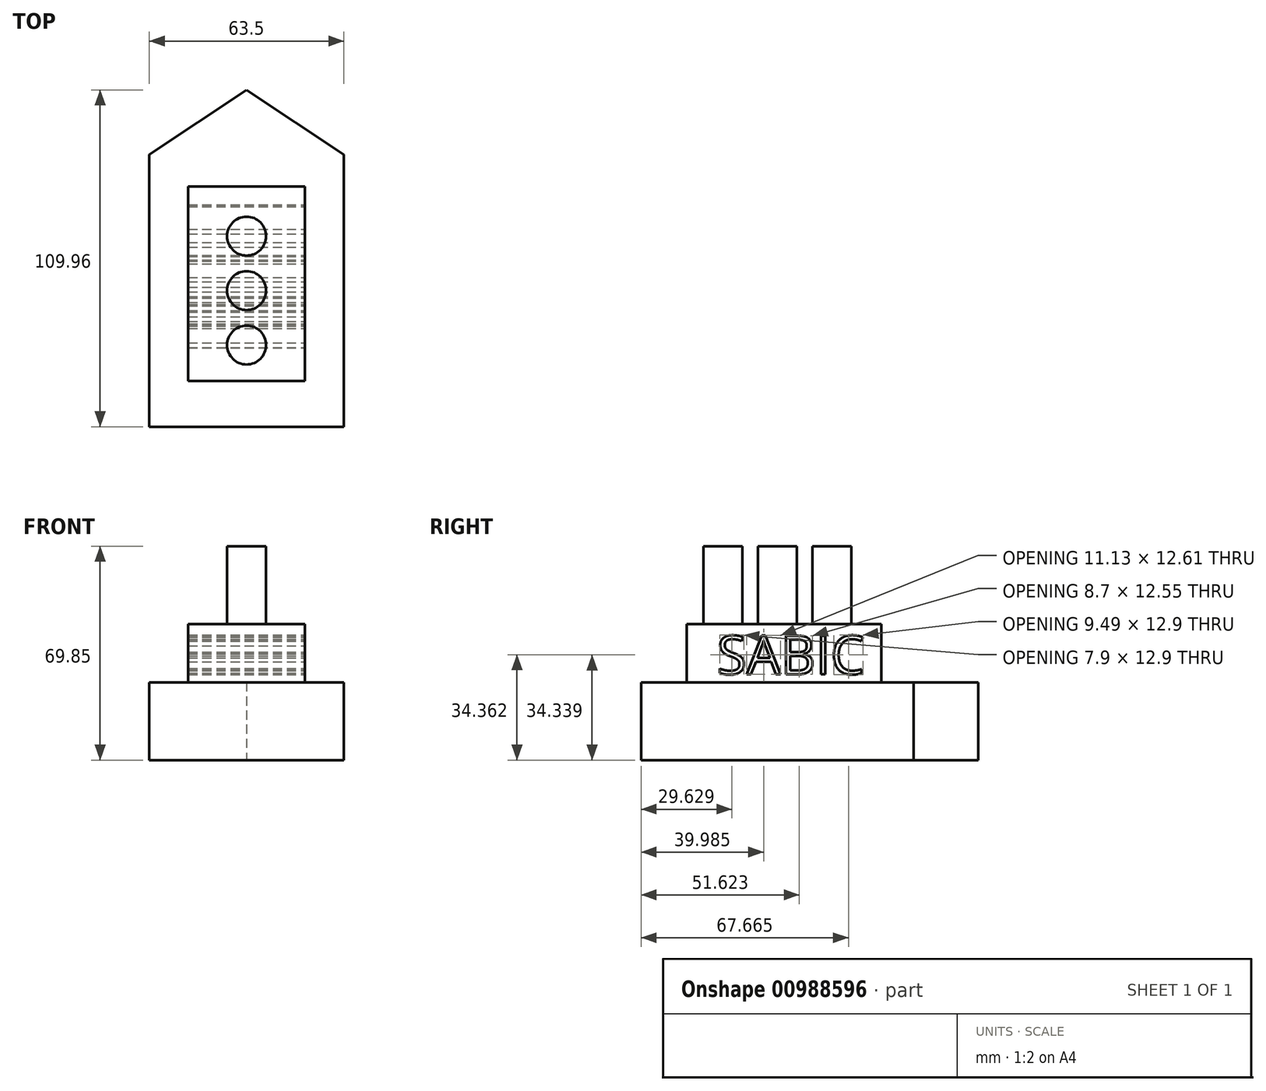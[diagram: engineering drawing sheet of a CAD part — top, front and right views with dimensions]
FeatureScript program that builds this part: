
annotation { "Feature Type Name" : "Feature", "Feature Type Description" : "" }
export const myFeature = defineFeature(function(context is Context, id is Id, definition is map)
    precondition{}
    {
        {
            var Q0;
            Q0=qCreatedBy(makeId("Top.planeOp"),FACE);
            var sketch = newSketch(context, id + "F0", { "sketchPlane" : qUnion([Q0])});
            skLineSegment(sketch, "E0", {"start": v(-31.75, 38.66) * mm, "end": v(-31.75, -50.24) * mm});
            skLineSegment(sketch, "E1", {"start": v(-31.75, -50.24) * mm, "end": v(31.75, -50.24) * mm});
            skLineSegment(sketch, "E2", {"start": v(31.75, -50.24) * mm, "end": v(31.75, 38.66) * mm});
            skLineSegment(sketch, "E3", {"start": v(31.75, 38.66) * mm, "end": v(0, 59.72) * mm});
            skLineSegment(sketch, "E4", {"start": v(0, 59.72) * mm, "end": v(-31.75, 38.66) * mm});
            skSolve(sketch);
        }
        {
            var Q0;
            Q0 = qSketchRegion(id + "F0", true);
            extrude(context, id + "F1", {"entities" : qUnion([Q0]), "depth" : 25.4 * mm, "offsetDistance" : 25.4 * mm});
        }
        {
            var Q0;
            Q0=makeQuery(id+"F1.opExtrude","CAP_FACE",FACE,{"disambiguationData":[OSD([sQuery(id+"F0.wireOp",EDGE,"E0"),sQuery(id+"F0.wireOp",EDGE,"E1"),sQuery(id+"F0.wireOp",EDGE,"E2"),sQuery(id+"F0.wireOp",EDGE,"E3"),sQuery(id+"F0.wireOp",EDGE,"E4")])],"isStart":false});
            var sketch = newSketch(context, id + "F2", { "sketchPlane" : qUnion([Q0])});
            skLineSegment(sketch, "E5.bottom", {"start": v(-19.05, 28.15) * mm, "end": v(19.05, 28.15) * mm});
            skLineSegment(sketch, "E5.top", {"start": v(-19.05, -35.35) * mm, "end": v(19.05, -35.35) * mm});
            skLineSegment(sketch, "E5.left", {"start": v(-19.05, 28.15) * mm, "end": v(-19.05, -35.35) * mm});
            skLineSegment(sketch, "E5.right", {"start": v(19.05, 28.15) * mm, "end": v(19.05, -35.35) * mm});
            skSolve(sketch);
        }
        {
            var Q0;
            Q0 = qSketchRegion(id + "F2", true);
            extrude(context, id + "F3", {"entities" : qUnion([Q0]), "operationType" : NewBodyOperationType.ADD, "depth" : 19.05 * mm, "offsetDistance" : 25.4 * mm});
        }
        {
            var Q0;
            Q0=makeQuery(id+"F3.opExtrude","CAP_FACE",FACE,{"disambiguationData":[OSD([sQuery(id+"F2.wireOp",EDGE,"E5.bottom"),sQuery(id+"F2.wireOp",EDGE,"E5.top"),sQuery(id+"F2.wireOp",EDGE,"E5.left"),sQuery(id+"F2.wireOp",EDGE,"E5.right")])],"isStart":false});
            var sketch = newSketch(context, id + "F4", { "sketchPlane" : qUnion([Q0])});
            skCircle(sketch, "E6", {"center": v(0, 11.99) * mm, "radius": 6.35 * mm});
            skCircle(sketch, "E7", {"center": v(0, -5.8) * mm, "radius": 6.35 * mm});
            skCircle(sketch, "E8", {"center": v(0, -23.57) * mm, "radius": 6.35 * mm});
            skSolve(sketch);
        }
        {
            var Q0;
            Q0 = qSketchRegion(id + "F4", true);
            extrude(context, id + "F5", {"entities" : qUnion([Q0]), "operationType" : NewBodyOperationType.ADD, "depth" : 25.4 * mm, "offsetDistance" : 25.4 * mm});
        }
        {
            var Q0;
            Q0=makeQuery(id+"F3.opExtrude","SWEPT_FACE",FACE,{"disambiguationData":[OSD([sQuery(id+"F2.wireOp",EDGE,"E5.right")])]});
            var sketch = newSketch(context, id + "F6", { "sketchPlane" : qUnion([Q0])});
            skText(sketch, "E9", { "text": "SABIC", "fontName": "OpenSans-Regular.ttf"});
            const initialGuessF6  = {"E9": [-0.02547, 0.02806, 1, 0, 0.01266]};
            skSetInitialGuess(sketch, initialGuessF6);
            skSolve(sketch);
        }
        {
            var Q0;
            Q0 = qSketchRegion(id + "F6", true);
            extrude(context, id + "F7", {"entities" : qUnion([Q0]), "operationType" : NewBodyOperationType.REMOVE, "oppositeDirection" : true, "depth" : 40.13 * mm, "offsetDistance" : 25.4 * mm});
        }
    });
